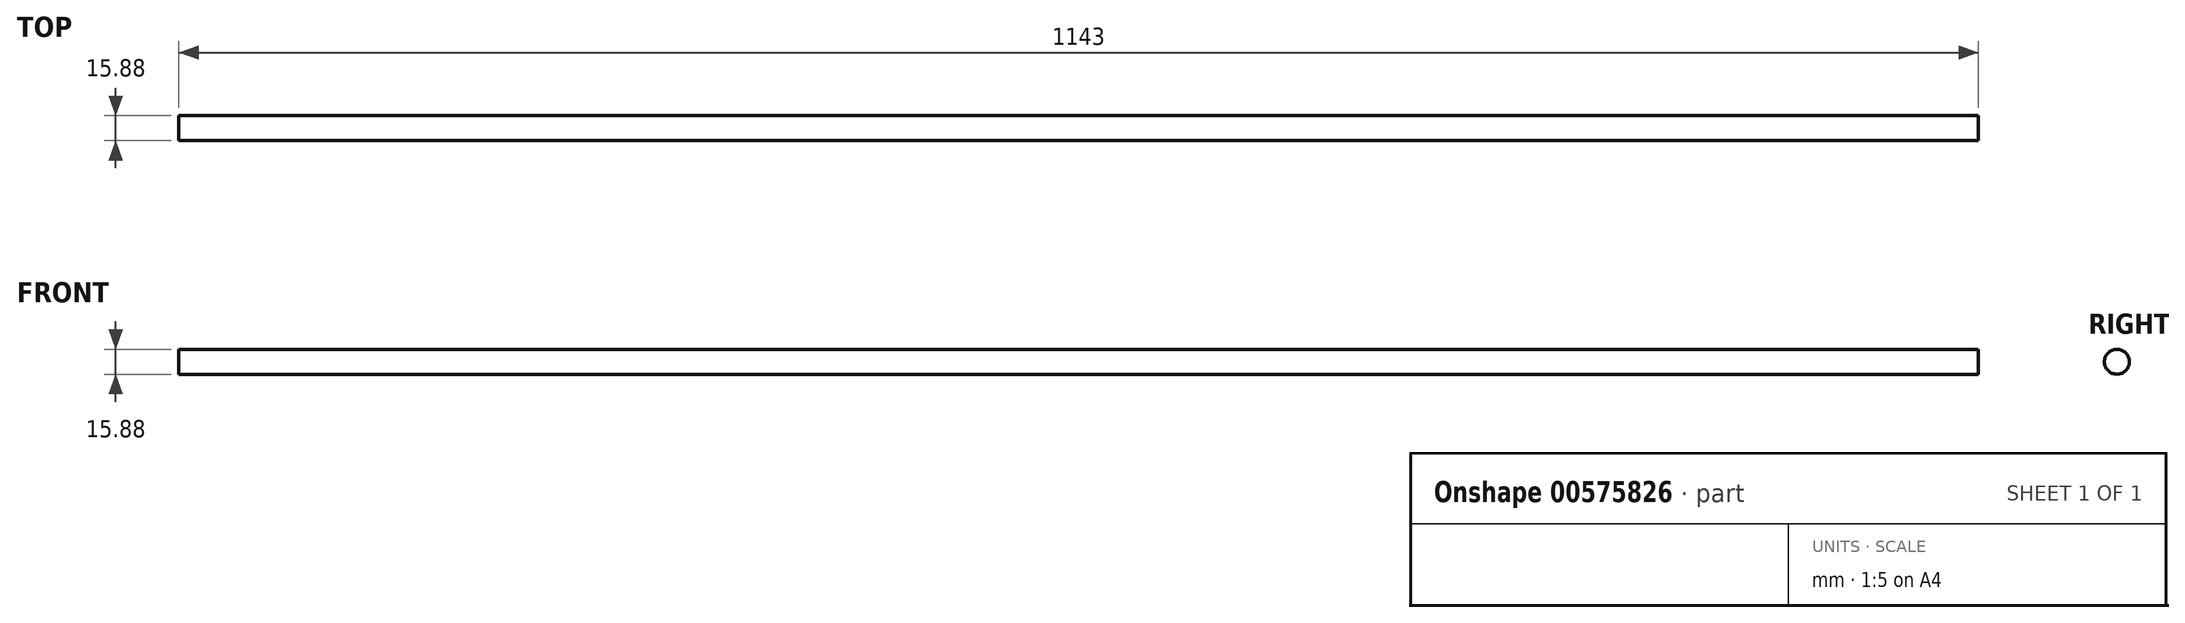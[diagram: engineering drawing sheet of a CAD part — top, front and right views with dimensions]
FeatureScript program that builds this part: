
annotation { "Feature Type Name" : "Feature", "Feature Type Description" : "" }
export const myFeature = defineFeature(function(context is Context, id is Id, definition is map)
    precondition{}
    {
        {
            var Q0;
            Q0=qCreatedBy(makeId("Top.planeOp"),FACE);
            var sketch = newSketch(context, id + "F0", { "sketchPlane" : qUnion([Q0])});
            skLineSegment(sketch, "E0.bottom", {"start": v(0, 7.94) * mm, "end": v(1143, 7.94) * mm});
            skLineSegment(sketch, "E0.top", {"start": v(0, 0) * mm, "end": v(1143, 0) * mm});
            skLineSegment(sketch, "E0.left", {"start": v(0, 7.94) * mm, "end": v(0, 0) * mm});
            skLineSegment(sketch, "E0.right", {"start": v(1143, 7.94) * mm, "end": v(1143, 0) * mm});
            skSolve(sketch);
        }
        {
            var Q0;
            Q0=makeQuery(id+"F0.imprint","IMPRINT",FACE,{"disambiguationData":[TD([[makeQuery(id+"F0.imprint","IMPRINT",EDGE,{"derivedFrom":sQuery(id+"F0.wireOp",EDGE,"E0.bottom")}),-1.0]])]});
            var Q1;
            Q1=sQuery(id+"F0.wireOp",EDGE,"E0.bottom");
            revolve(context, id + "F1", {"entities" : qUnion([Q0]), "axis" : qUnion([Q1]), "revolveType" : RevolveType.FULL, "surfaceOperationType" : NewSurfaceOperationType.NEW});
        }
    });
